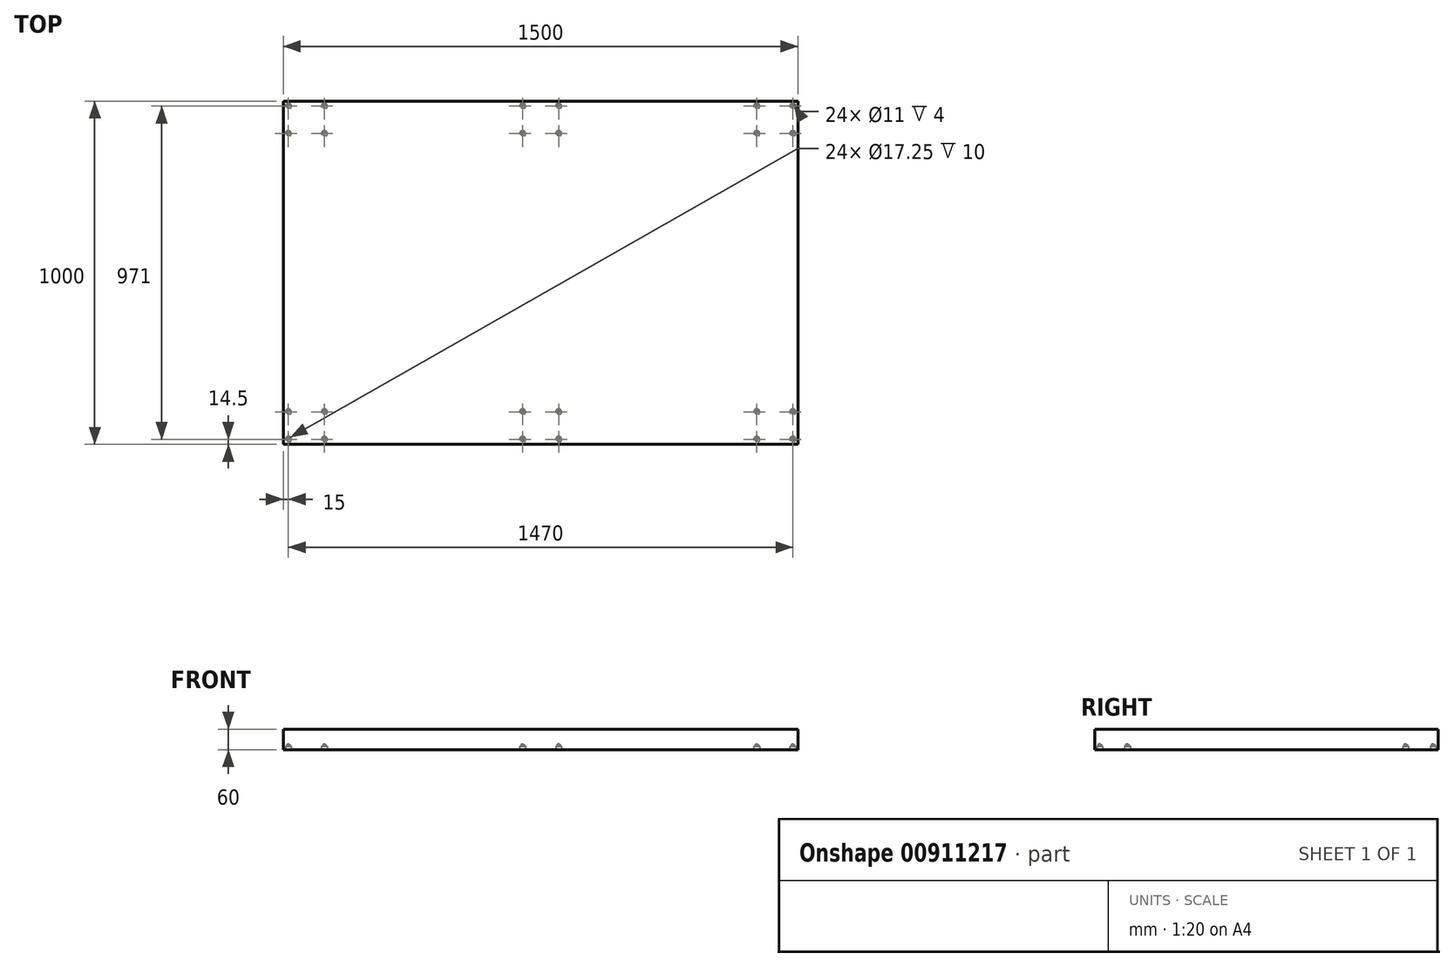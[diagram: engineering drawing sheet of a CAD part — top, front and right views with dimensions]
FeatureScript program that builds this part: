
annotation { "Feature Type Name" : "Feature", "Feature Type Description" : "" }
export const myFeature = defineFeature(function(context is Context, id is Id, definition is map)
    precondition{}
    {
        {
            var Q0;
            Q0=qCreatedBy(makeId("Top.planeOp"),FACE);
            var sketch = newSketch(context, id + "F0", { "sketchPlane" : qUnion([Q0])});
            skLineSegment(sketch, "E0.bottom", {"start": v(750, 500) * mm, "end": v(-750, 500) * mm});
            skLineSegment(sketch, "E0.top", {"start": v(750, -500) * mm, "end": v(-750, -500) * mm});
            skLineSegment(sketch, "E0.left", {"start": v(750, 500) * mm, "end": v(750, -500) * mm});
            skLineSegment(sketch, "E0.right", {"start": v(-750, 500) * mm, "end": v(-750, -500) * mm});
            skPoint(sketch, "E0.middle", {"position": v(0, 0) * mm});
            skSolve(sketch);
        }
        {
            var Q0;
            Q0=makeQuery(id+"F0.imprint","IMPRINT",FACE,{"disambiguationData":[TD([[makeQuery(id+"F0.imprint","IMPRINT",EDGE,{"derivedFrom":sQuery(id+"F0.wireOp",EDGE,"E0.bottom")}),1.0]])]});
            extrude(context, id + "F1", {"entities" : qUnion([Q0]), "depth" : 60 * mm, "offsetDistance" : 25 * mm});
        }
        {
            var Q0;
            Q0=makeQuery(id+"F1.opExtrude","CAP_FACE",FACE,{"disambiguationData":[OSD([sQuery(id+"F0.wireOp",EDGE,"E0.bottom"),sQuery(id+"F0.wireOp",EDGE,"E0.top"),sQuery(id+"F0.wireOp",EDGE,"E0.left"),sQuery(id+"F0.wireOp",EDGE,"E0.right")])],"isStart":true});
            var sketch = newSketch(context, id + "F2", { "sketchPlane" : qUnion([Q0])});
            skLineSegment(sketch, "E1.bottom", {"start": v(-750, 500) * mm, "end": v(-615, 500) * mm});
            skLineSegment(sketch, "E1.top", {"start": v(-750, 391) * mm, "end": v(-615, 391) * mm});
            skLineSegment(sketch, "E1.left", {"start": v(-750, 500) * mm, "end": v(-750, 391) * mm});
            skLineSegment(sketch, "E1.right", {"start": v(-615, 500) * mm, "end": v(-615, 391) * mm});
            skLineSegment(sketch, "E2", {"start": v(-735, 485.5) * mm, "end": v(-630, 485.5) * mm});
            skLineSegment(sketch, "E3", {"start": v(-735, 485.5) * mm, "end": v(-735, 405.5) * mm});
            skCircle(sketch, "E4", {"center": v(-735, 485.5) * mm, "radius": 5 * mm});
            skCircle(sketch, "E5", {"center": v(-735, 405.5) * mm, "radius": 5 * mm});
            skCircle(sketch, "E6", {"center": v(-630, 485.5) * mm, "radius": 5 * mm});
            skLineSegment(sketch, "E7", {"start": v(-630, 485.5) * mm, "end": v(-630, 405.5) * mm});
            skCircle(sketch, "E8", {"center": v(-630, 405.5) * mm, "radius": 5 * mm});
            skLineSegment(sketch, "E9", {"start": v(-750, 500) * mm, "end": v(0, 500) * mm});
            skLineSegment(sketch, "E10", {"start": v(0, 500) * mm, "end": v(-69, 500) * mm});
            skLineSegment(sketch, "E11", {"start": v(0, 500) * mm, "end": v(69, 500) * mm});
            skLineSegment(sketch, "E12", {"start": v(69, 500) * mm, "end": v(69, 391) * mm});
            skLineSegment(sketch, "E13", {"start": v(69, 391) * mm, "end": v(-69, 391) * mm});
            skLineSegment(sketch, "E14", {"start": v(-69, 391) * mm, "end": v(-69, 500) * mm});
            skLineSegment(sketch, "E15", {"start": v(-52.5, 485.5) * mm, "end": v(52.5, 485.5) * mm});
            skLineSegment(sketch, "E16", {"start": v(52.5, 485.5) * mm, "end": v(52.5, 405.5) * mm});
            skLineSegment(sketch, "E17", {"start": v(-52.5, 485.5) * mm, "end": v(-52.5, 405.5) * mm});
            skCircle(sketch, "E18", {"center": v(-52.5, 485.5) * mm, "radius": 5 * mm});
            skCircle(sketch, "E19", {"center": v(-52.5, 405.5) * mm, "radius": 5 * mm});
            skCircle(sketch, "E20", {"center": v(52.5, 405.5) * mm, "radius": 5 * mm});
            skCircle(sketch, "E21", {"center": v(52.5, 485.5) * mm, "radius": 5 * mm});
            skLineSegment(sketch, "E22.bottom", {"start": v(750, 500) * mm, "end": v(615, 500) * mm});
            skLineSegment(sketch, "E22.top", {"start": v(750, 391) * mm, "end": v(615, 391) * mm});
            skLineSegment(sketch, "E22.left", {"start": v(750, 500) * mm, "end": v(750, 391) * mm});
            skLineSegment(sketch, "E22.right", {"start": v(615, 500) * mm, "end": v(615, 391) * mm});
            skLineSegment(sketch, "E23", {"start": v(630, 485.5) * mm, "end": v(735, 485.5) * mm});
            skLineSegment(sketch, "E24", {"start": v(735, 485.5) * mm, "end": v(735, 405.5) * mm});
            skLineSegment(sketch, "E25", {"start": v(735, 405.5) * mm, "end": v(630, 405.5) * mm});
            skCircle(sketch, "E26", {"center": v(630, 485.5) * mm, "radius": 5 * mm});
            skCircle(sketch, "E27", {"center": v(735, 485.5) * mm, "radius": 5 * mm});
            skCircle(sketch, "E28", {"center": v(735, 405.5) * mm, "radius": 5 * mm});
            skCircle(sketch, "E29", {"center": v(630, 405.5) * mm, "radius": 5 * mm});
            skLineSegment(sketch, "E30.0.1.0", {"start": v(-69, -500) * mm, "end": v(-69, -391) * mm});
            skLineSegment(sketch, "E30.0.1.1", {"start": v(-750, -391) * mm, "end": v(0, -391) * mm});
            skLineSegment(sketch, "E30.0.1.2", {"start": v(-750, -500) * mm, "end": v(-615, -500) * mm});
            skLineSegment(sketch, "E30.0.1.3", {"start": v(615, -391) * mm, "end": v(615, -500) * mm});
            skLineSegment(sketch, "E30.0.1.4", {"start": v(0, -391) * mm, "end": v(69, -391) * mm});
            skLineSegment(sketch, "E30.0.1.5", {"start": v(52.5, -405.5) * mm, "end": v(52.5, -485.5) * mm});
            skLineSegment(sketch, "E30.0.1.6", {"start": v(-52.5, -405.5) * mm, "end": v(52.5, -405.5) * mm});
            skLineSegment(sketch, "E30.0.1.7", {"start": v(-750, -391) * mm, "end": v(-750, -500) * mm});
            skLineSegment(sketch, "E30.0.1.8", {"start": v(750, -391) * mm, "end": v(750, -500) * mm});
            skLineSegment(sketch, "E30.0.1.9", {"start": v(735, -485.5) * mm, "end": v(630, -485.5) * mm});
            skLineSegment(sketch, "E30.0.1.10", {"start": v(750, -500) * mm, "end": v(615, -500) * mm});
            skLineSegment(sketch, "E30.0.1.11", {"start": v(750, -391) * mm, "end": v(615, -391) * mm});
            skLineSegment(sketch, "E30.0.1.12", {"start": v(-615, -391) * mm, "end": v(-615, -500) * mm});
            skLineSegment(sketch, "E30.0.1.13", {"start": v(-52.5, -405.5) * mm, "end": v(-52.5, -485.5) * mm});
            skLineSegment(sketch, "E30.0.1.14", {"start": v(630, -405.5) * mm, "end": v(735, -405.5) * mm});
            skLineSegment(sketch, "E30.0.1.15", {"start": v(-735, -405.5) * mm, "end": v(-735, -485.5) * mm});
            skLineSegment(sketch, "E30.0.1.16", {"start": v(735, -405.5) * mm, "end": v(735, -485.5) * mm});
            skLineSegment(sketch, "E30.0.1.17", {"start": v(69, -391) * mm, "end": v(69, -500) * mm});
            skLineSegment(sketch, "E30.0.1.18", {"start": v(-630, -405.5) * mm, "end": v(-630, -485.5) * mm});
            skLineSegment(sketch, "E30.0.1.19", {"start": v(-735, -405.5) * mm, "end": v(-630, -405.5) * mm});
            skLineSegment(sketch, "E30.0.1.20", {"start": v(-750, -391) * mm, "end": v(-615, -391) * mm});
            skLineSegment(sketch, "E30.0.1.21", {"start": v(0, -391) * mm, "end": v(-69, -391) * mm});
            skLineSegment(sketch, "E30.0.1.22", {"start": v(69, -500) * mm, "end": v(-69, -500) * mm});
            skCircle(sketch, "E30.0.1.23", {"center": v(-52.5, -485.5) * mm, "radius": 5 * mm});
            skCircle(sketch, "E30.0.1.24", {"center": v(630, -485.5) * mm, "radius": 5 * mm});
            skCircle(sketch, "E30.0.1.25", {"center": v(-735, -485.5) * mm, "radius": 5 * mm});
            skCircle(sketch, "E30.0.1.26", {"center": v(-630, -485.5) * mm, "radius": 5 * mm});
            skCircle(sketch, "E30.0.1.27", {"center": v(52.5, -485.5) * mm, "radius": 5 * mm});
            skCircle(sketch, "E30.0.1.28", {"center": v(52.5, -405.5) * mm, "radius": 5 * mm});
            skCircle(sketch, "E30.0.1.29", {"center": v(735, -485.5) * mm, "radius": 5 * mm});
            skCircle(sketch, "E30.0.1.30", {"center": v(735, -405.5) * mm, "radius": 5 * mm});
            skCircle(sketch, "E30.0.1.31", {"center": v(630, -405.5) * mm, "radius": 5 * mm});
            skCircle(sketch, "E30.0.1.32", {"center": v(-52.5, -405.5) * mm, "radius": 5 * mm});
            skCircle(sketch, "E30.0.1.33", {"center": v(-630, -405.5) * mm, "radius": 5 * mm});
            skCircle(sketch, "E30.0.1.34", {"center": v(-735, -405.5) * mm, "radius": 5 * mm});
            skLineSegment(sketch, "E30.direction1", {"start": v(-750, 391) * mm, "end": v(-647.4, 391) * mm, "construction": true});
            skLineSegment(sketch, "E30.direction2", {"start": v(-750, 391) * mm, "end": v(-750, -500) * mm, "construction": true});
            skSolve(sketch);
        }
        {
            var Q0;
            Q0=sQuery(id+"F2.wireOp",VERTEX,"E2.start");
            var Q1;
            Q1=sQuery(id+"F2.wireOp",VERTEX,"E3.end");
            var Q2;
            Q2=sQuery(id+"F2.wireOp",VERTEX,"E7.end");
            var Q3;
            Q3=sQuery(id+"F2.wireOp",VERTEX,"E2.end");
            var Q4;
            Q4=sQuery(id+"F2.wireOp",VERTEX,"E15.end");
            var Q5;
            Q5=sQuery(id+"F2.wireOp",VERTEX,"E15.start");
            var Q6;
            Q6=sQuery(id+"F2.wireOp",VERTEX,"E17.end");
            var Q7;
            Q7=sQuery(id+"F2.wireOp",VERTEX,"E16.end");
            var Q8;
            Q8=sQuery(id+"F2.wireOp",VERTEX,"E24.end");
            var Q9;
            Q9=sQuery(id+"F2.wireOp",VERTEX,"E23.end");
            var Q10;
            Q10=sQuery(id+"F2.wireOp",VERTEX,"E23.start");
            var Q11;
            Q11=sQuery(id+"F2.wireOp",VERTEX,"E25.end");
            var Q12;
            Q12=sQuery(id+"F2.wireOp",VERTEX,"E30.0.1.15.end");
            var Q13;
            Q13=sQuery(id+"F2.wireOp",VERTEX,"E30.0.1.15.start");
            var Q14;
            Q14=sQuery(id+"F2.wireOp",VERTEX,"E30.0.1.18.start");
            var Q15;
            Q15=sQuery(id+"F2.wireOp",VERTEX,"E30.0.1.18.end");
            var Q16;
            Q16=sQuery(id+"F2.wireOp",VERTEX,"E30.0.1.13.end");
            var Q17;
            Q17=sQuery(id+"F2.wireOp",VERTEX,"E30.0.1.6.start");
            var Q18;
            Q18=sQuery(id+"F2.wireOp",VERTEX,"E30.0.1.5.end");
            var Q19;
            Q19=sQuery(id+"F2.wireOp",VERTEX,"E30.0.1.5.start");
            var Q20;
            Q20=sQuery(id+"F2.wireOp",VERTEX,"E30.0.1.9.end");
            var Q21;
            Q21=sQuery(id+"F2.wireOp",VERTEX,"E30.0.1.14.start");
            var Q22;
            Q22=sQuery(id+"F2.wireOp",VERTEX,"E30.0.1.14.end");
            var Q23;
            Q23=sQuery(id+"F2.wireOp",VERTEX,"E30.0.1.9.start");
            var Q24;
            Q24=makeQuery(id+"F1.opExtrude","SWEPT_BODY",BODY,{"disambiguationData":[OSD([sQuery(id+"F0.wireOp",EDGE,"E0.bottom"),sQuery(id+"F0.wireOp",EDGE,"E0.top"),sQuery(id+"F0.wireOp",EDGE,"E0.left"),sQuery(id+"F0.wireOp",EDGE,"E0.right")])]});
            hole(context, id + "F3", {"style" : HoleStyle.C_BORE, "endStyle" : HoleEndStyle.BLIND, "standardTappedOrClearance" : lookupTablePath({ "fit" : "Normal", "standard" : "ISO", "size" : "M10", "type" : "Clearance" }), "standardBlindInLast" : lookupTablePath({ "fit" : "Normal", "standard" : "ISO", "size" : "M10", "type" : "Clearance" }), "holeDiameter" : 11 * mm, "cBoreDiameter" : 17.25 * mm, "cBoreDepth" : 10 * mm, "majorDiameter" : 5 * mm, "holeDepth" : 14 * mm, "isTappedThrough" : true, "tappedDepth" : 12 * mm, "tapClearance" : 3, "locations" : qUnion([Q0, Q1, Q2, Q3, Q4, Q5, Q6, Q7, Q8, Q9, Q10, Q11, Q12, Q13, Q14, Q15, Q16, Q17, Q18, Q19, Q20, Q21, Q22, Q23]), "scope" : qUnion([Q24])});
        }
    });
